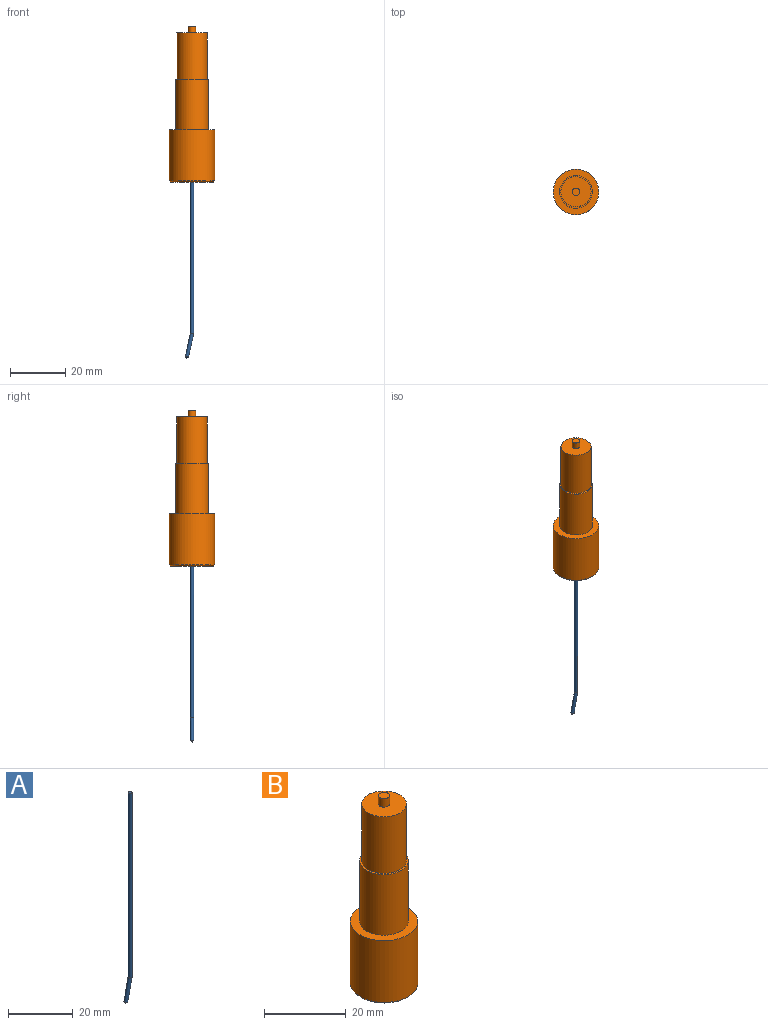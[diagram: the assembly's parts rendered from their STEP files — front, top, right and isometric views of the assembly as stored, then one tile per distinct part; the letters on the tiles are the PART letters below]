
ASSEMBLY  parts=2 mates=1
PART A: 7 faces, bbox 3x1.2x78.8 mm
  f0: cylinder r=0.6mm len=70mm, axis (0,0,-1), area 263.8mm2, adj f1,f2,f3
  f1: plane 1.2x0.6mm, normal (0,0,-1), area 0.6mm2, adj f0,f4
  f2: plane 1.2x1.2mm, normal (0,0,1), area 1.1mm2, adj f0
  f3: cylinder r=0.6mm len=8.56mm, axis (0.21,0,0.98), area 32mm2, adj f0,f4,f6
  f4: plane 1.2x0.59mm, normal (0.21,0,0.98), area 0.6mm2, adj f1,f3
  f5: plane 0.2x0.2mm, normal (-0.21,0,-0.98), area 0mm2, adj f6
  f6: cone r=0.1mm half-angle=45deg, axis (0.21,0,0.98), area 1.6mm2, adj f3,f5
PART B: 12 faces, bbox 16.5x16.5x56.6 mm
  f0: cylinder r=8.25mm len=18.5mm, axis (0,0,-1), area 959mm2, adj f1,f9
  f1: plane 16.5x16.5mm, normal (0,0,1), area 103mm2, adj f0,f3
  f2: plane 15.5x15.5mm, normal (0,0,-1), area 187.6mm2, adj f9,f10
  f3: cylinder r=5.94mm len=18.15mm, axis (0,0,-1), area 677.4mm2, adj f1,f4
  f4: plane 11.88x11.88mm, normal (0,0,1), area 17.2mm2, adj f3,f5
  f5: cylinder r=5.46mm len=16.95mm, axis (0,0,-1), area 581.5mm2, adj f4,f6
  f6: plane 10.92x10.92mm, normal (0,0,1), area 87.8mm2, adj f5,f7
  f7: cylinder r=1.36mm len=2.73mm, axis (0,0,-1), area 21.4mm2, adj f6,f8
  f8: plane 2.73x2.73mm, normal (0,0,1), area 5.9mm2, adj f7
  f9: cone r=8.25mm half-angle=45deg, axis (0,0,1), area 35.5mm2, adj f0,f2
  f10: cylinder r=0.6mm len=15mm, axis (0,0,-1), area 56.5mm2, adj f2,f11
  f11: plane 1.2x1.2mm, normal (0,0,-1), area 1.1mm2, adj f10
PLACE A t=(13.73,18.1,-14.54)mm
PLACE B t=(13.73,18.1,40.46)mm
MATE fastened B.f10 <-> A.f0  axis (0,0,-1) through (13.73,18.1,55.46)mm
